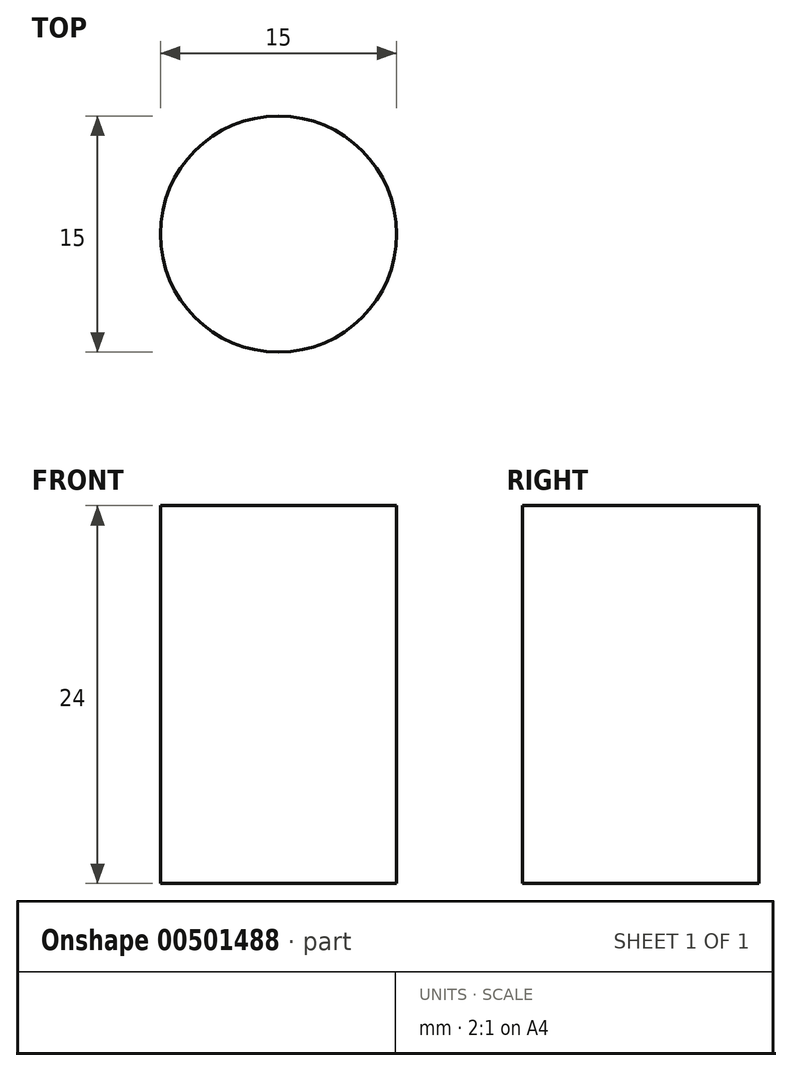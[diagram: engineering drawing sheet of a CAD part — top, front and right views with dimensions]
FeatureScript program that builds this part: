
annotation { "Feature Type Name" : "Feature", "Feature Type Description" : "" }
export const myFeature = defineFeature(function(context is Context, id is Id, definition is map)
    precondition{}
    {
        {
            var Q0;
            Q0=qCreatedBy(makeId("Top.planeOp"),FACE);
            var sketch = newSketch(context, id + "F0", { "sketchPlane" : qUnion([Q0])});
            skCircle(sketch, "E0", {"center": v(0, 0) * mm, "radius": 7.5 * mm});
            skSolve(sketch);
        }
        {
            var Q0;
            Q0 = qSketchRegion(id + "F0", true);
            extrude(context, id + "F1", {"entities" : qUnion([Q0]), "depth" : 24 * mm, "offsetDistance" : 25 * mm});
        }
    });
